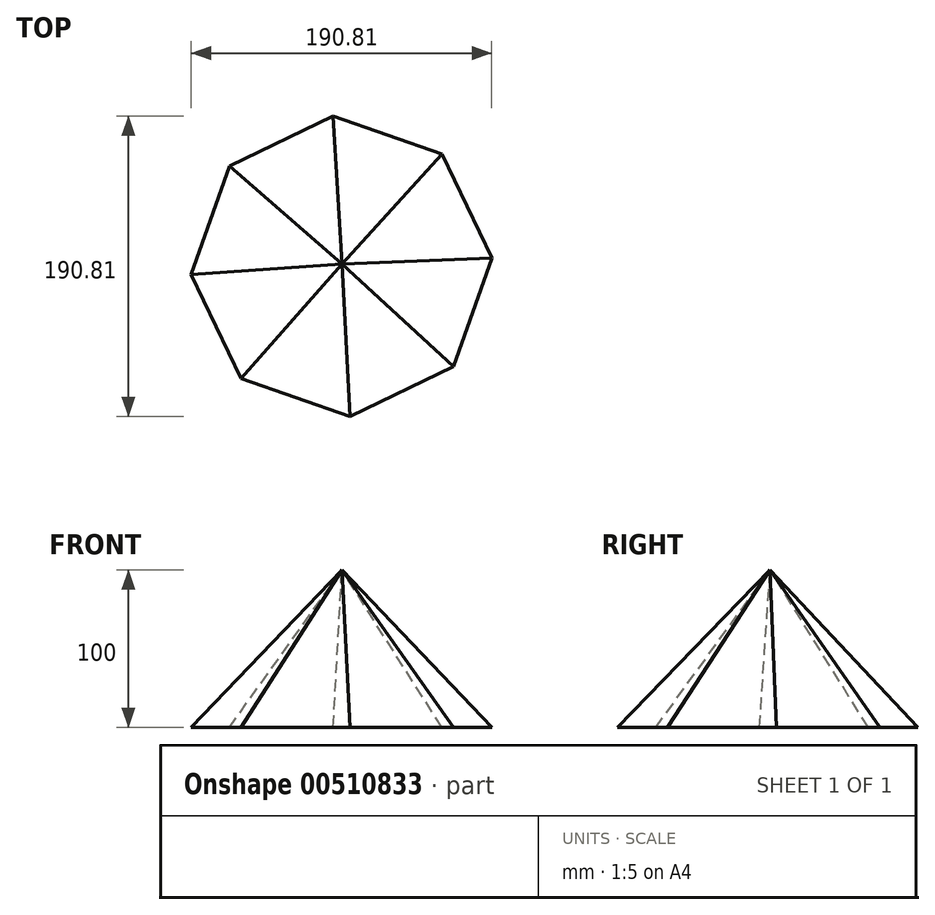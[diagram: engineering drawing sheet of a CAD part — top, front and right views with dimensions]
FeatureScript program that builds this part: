
annotation { "Feature Type Name" : "Feature", "Feature Type Description" : "" }
export const myFeature = defineFeature(function(context is Context, id is Id, definition is map)
    precondition{}
    {
        {
            var Q0;
            Q0=qCreatedBy(makeId("Top.planeOp"),FACE);
            var sketch = newSketch(context, id + "F0", { "sketchPlane" : qUnion([Q0])});
            skCircle(sketch, "E0.cCircle", {"center": v(-3.46, 8.9) * mm, "radius": 95.55 * mm, "construction": true});
            skLineSegment(sketch, "E0.0", {"start": v(1.85, -86.5) * mm, "end": v(-67.17, -62.32) * mm});
            skLineSegment(sketch, "E0.1", {"start": v(-67.17, -62.32) * mm, "end": v(-98.87, 3.59) * mm});
            skLineSegment(sketch, "E0.2", {"start": v(-98.87, 3.59) * mm, "end": v(-74.68, 72.6) * mm});
            skLineSegment(sketch, "E0.3", {"start": v(-74.68, 72.6) * mm, "end": v(-8.77, 104.3) * mm});
            skLineSegment(sketch, "E0.4", {"start": v(-8.77, 104.3) * mm, "end": v(60.25, 80.11) * mm});
            skLineSegment(sketch, "E0.5", {"start": v(60.25, 80.11) * mm, "end": v(91.94, 14.2) * mm});
            skLineSegment(sketch, "E0.6", {"start": v(91.94, 14.2) * mm, "end": v(67.75, -54.81) * mm});
            skLineSegment(sketch, "E0.7", {"start": v(67.75, -54.81) * mm, "end": v(1.85, -86.5) * mm});
            skPoint(sketch, "E1", {"position": v(-3.74, 8.43) * mm});
            skSolve(sketch);
        }
        {
            var Q0;
            Q0=qCreatedBy(makeId("Top.planeOp"),FACE);
            cPlane(context, id + "F1", {"entities" : qUnion([Q0]), "cplaneType" : CPlaneType.OFFSET, "offset" : 100 * mm, "width" : 150 * mm, "height" : 150 * mm});
        }
        {
            var Q0;
            Q0=qCreatedBy(id+"F1.planeOp",FACE);
            var sketch = newSketch(context, id + "F2", { "sketchPlane" : qUnion([Q0])});
            skPoint(sketch, "E2", {"position": v(-3.27, 10.29) * mm});
            skSolve(sketch);
        }
        {
            var Q0;
            Q0=makeQuery(id+"F0.imprint","IMPRINT",FACE,{"disambiguationData":[TD([[makeQuery(id+"F0.imprint","IMPRINT",EDGE,{"derivedFrom":sQuery(id+"F0.wireOp",EDGE,"E0.0")}),-1.0]])]});
            var Q1;
            Q1=sQuery(id+"F2.wireOp",VERTEX,"E2");
            loft(context, id + "F3", {"sheetProfilesArray" : [{ "sheetProfileEntities" : qUnion([Q0]) }, { "sheetProfileEntities" : qUnion([Q1]) }]});
        }
    });
